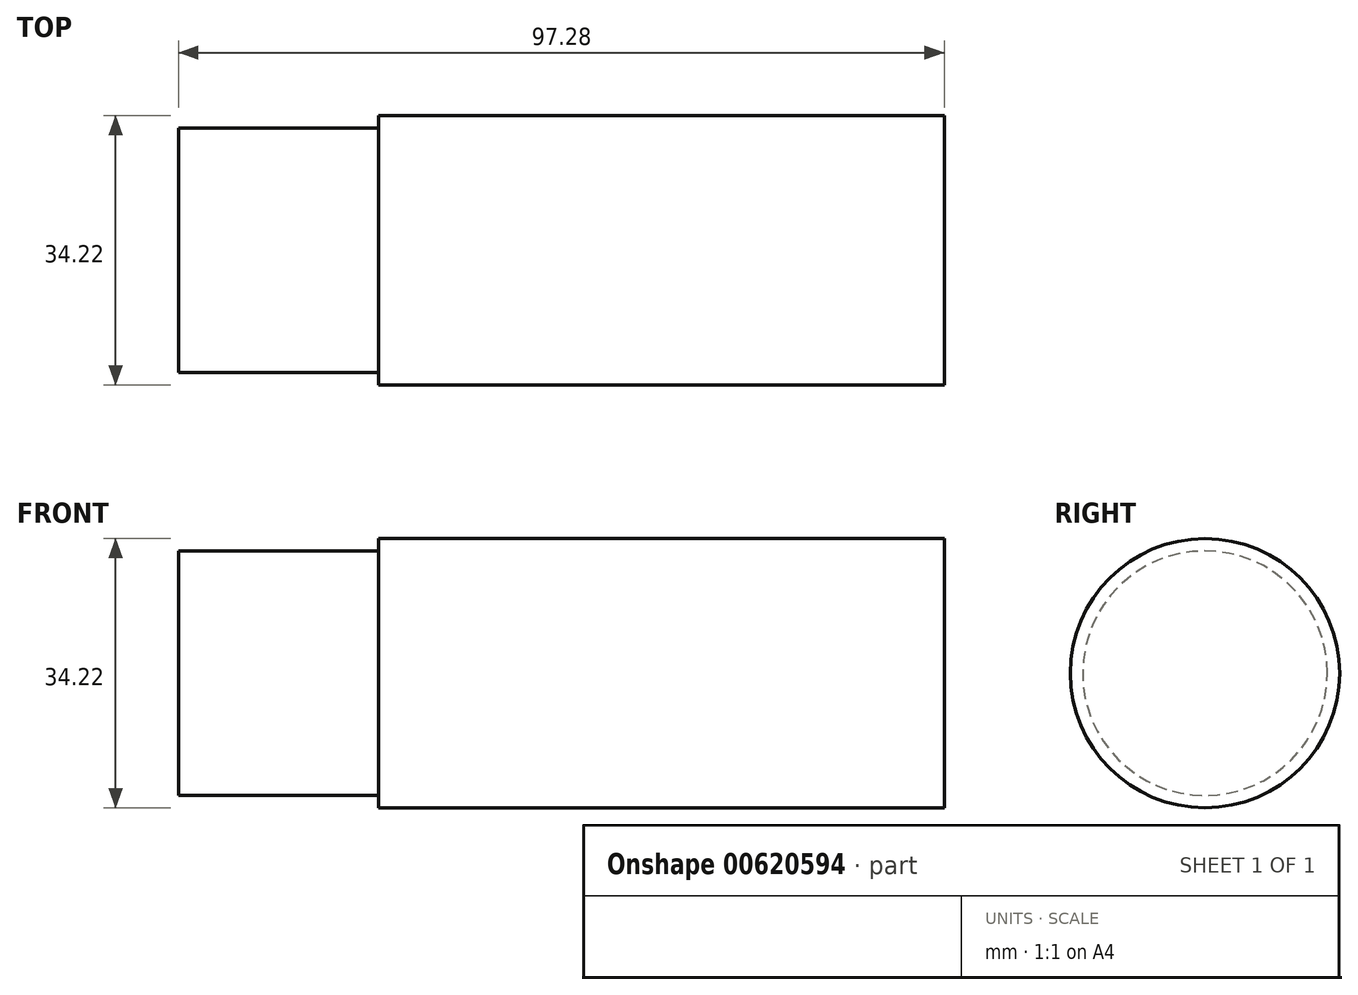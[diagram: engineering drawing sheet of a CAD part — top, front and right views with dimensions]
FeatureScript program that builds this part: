
annotation { "Feature Type Name" : "Feature", "Feature Type Description" : "" }
export const myFeature = defineFeature(function(context is Context, id is Id, definition is map)
    precondition{}
    {
        {
            var Q0;
            Q0=qCreatedBy(makeId("Right.planeOp"),FACE);
            var sketch = newSketch(context, id + "F0", { "sketchPlane" : qUnion([Q0])});
            skCircle(sketch, "E0", {"center": v(0, 0) * mm, "radius": 17.1 * mm});
            skSolve(sketch);
        }
        {
            var Q0;
            Q0=makeQuery(id+"F0.imprint","IMPRINT",FACE,{"disambiguationData":[TD([[makeQuery(id+"F0.imprint","IMPRINT",EDGE,{"derivedFrom":sQuery(id+"F0.wireOp",EDGE,"E0")}),1.0]])]});
            extrude(context, id + "F1", {"entities" : qUnion([Q0]), "depth" : 97.28 * mm, "offsetDistance" : 25.4 * mm});
        }
        {
            var Q0;
            Q0=makeQuery(id+"F1.opExtrude","CAP_FACE",FACE,{"disambiguationData":[OSD([sQuery(id+"F0.wireOp",EDGE,"E0")])],"isStart":true});
            var sketch = newSketch(context, id + "F2", { "sketchPlane" : qUnion([Q0])});
            skCircle(sketch, "E1", {"center": v(0, 0) * mm, "radius": 15.54 * mm});
            skSolve(sketch);
        }
        {
            var Q0;
            Q0=makeQuery(id+"F2.imprint","IMPRINT",FACE,{"disambiguationData":[TD([[makeQuery(id+"F2.imprint","IMPRINT",EDGE,{"derivedFrom":sQuery(id+"F2.wireOp",EDGE,"E1")}),-1.0]])]});
            extrude(context, id + "F3", {"entities" : qUnion([Q0]), "operationType" : NewBodyOperationType.REMOVE, "oppositeDirection" : true, "depth" : 25.4 * mm, "offsetDistance" : 25.4 * mm});
        }
    });
